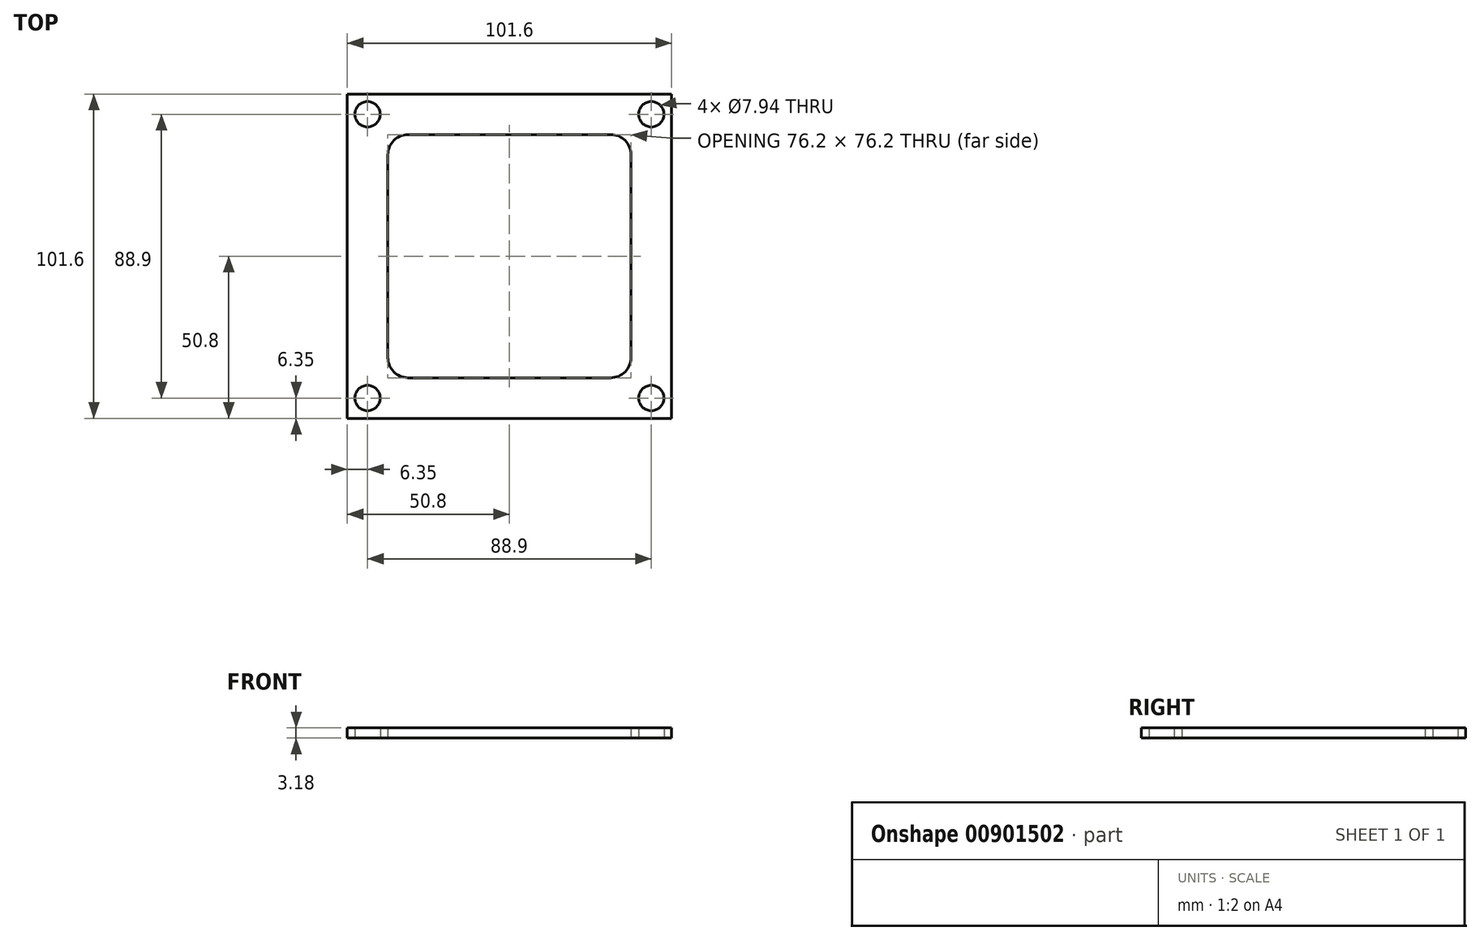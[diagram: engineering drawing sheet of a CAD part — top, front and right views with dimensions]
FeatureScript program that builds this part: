
annotation { "Feature Type Name" : "Feature", "Feature Type Description" : "" }
export const myFeature = defineFeature(function(context is Context, id is Id, definition is map)
    precondition{}
    {
        {
            var Q0;
            Q0=qCreatedBy(makeId("Top.planeOp"),FACE);
            var sketch = newSketch(context, id + "F0", { "sketchPlane" : qUnion([Q0])});
            skLineSegment(sketch, "E0.bottom", {"start": v(0, 0) * mm, "end": v(101.6, 0) * mm});
            skLineSegment(sketch, "E0.top", {"start": v(0, 101.6) * mm, "end": v(101.6, 101.6) * mm});
            skLineSegment(sketch, "E0.left", {"start": v(0, 0) * mm, "end": v(0, 101.6) * mm});
            skLineSegment(sketch, "E0.right", {"start": v(101.6, 0) * mm, "end": v(101.6, 101.6) * mm});
            skLineSegment(sketch, "E1.bottom", {"start": v(19.05, 12.7) * mm, "end": v(82.55, 12.7) * mm});
            skLineSegment(sketch, "E1.top", {"start": v(19.05, 88.9) * mm, "end": v(82.55, 88.9) * mm});
            skLineSegment(sketch, "E1.left", {"start": v(12.7, 19.05) * mm, "end": v(12.7, 82.55) * mm});
            skLineSegment(sketch, "E1.right", {"start": v(88.9, 19.05) * mm, "end": v(88.9, 82.55) * mm});
            skPoint(sketch, "E2.visualSharp", {"position": v(12.7, 12.7) * mm});
            skArc(sketch, "E2.filletArc", {"start": v(12.7, 19.05) * mm, "mid": v(14.56, 14.56) * mm, "end": v(19.05, 12.7) * mm});
            skPoint(sketch, "E3.visualSharp", {"position": v(88.9, 12.7) * mm});
            skArc(sketch, "E3.filletArc", {"start": v(82.55, 12.7) * mm, "mid": v(87.04, 14.56) * mm, "end": v(88.9, 19.05) * mm});
            skPoint(sketch, "E4.visualSharp", {"position": v(88.9, 88.9) * mm});
            skArc(sketch, "E4.filletArc", {"start": v(88.9, 82.55) * mm, "mid": v(87.04, 87.04) * mm, "end": v(82.55, 88.9) * mm});
            skPoint(sketch, "E5.visualSharp", {"position": v(12.7, 88.9) * mm});
            skArc(sketch, "E5.filletArc", {"start": v(19.05, 88.9) * mm, "mid": v(14.56, 87.04) * mm, "end": v(12.7, 82.55) * mm});
            skLineSegment(sketch, "E6", {"start": v(88.9, 12.7) * mm, "end": v(101.6, 0) * mm, "construction": true});
            skLineSegment(sketch, "E7", {"start": v(12.7, 12.7) * mm, "end": v(0, 0) * mm, "construction": true});
            skLineSegment(sketch, "E8", {"start": v(6.35, 6.35) * mm, "end": v(95.25, 6.35) * mm, "construction": true});
            skLineSegment(sketch, "E9", {"start": v(0, 101.6) * mm, "end": v(12.7, 88.9) * mm, "construction": true});
            skLineSegment(sketch, "E10", {"start": v(88.9, 88.9) * mm, "end": v(101.6, 101.6) * mm, "construction": true});
            skLineSegment(sketch, "E11", {"start": v(95.25, 95.25) * mm, "end": v(6.35, 95.25) * mm, "construction": true});
            skLineSegment(sketch, "E12", {"start": v(6.35, 95.25) * mm, "end": v(6.35, 6.35) * mm, "construction": true});
            skLineSegment(sketch, "E13", {"start": v(95.25, 6.35) * mm, "end": v(95.25, 95.25) * mm, "construction": true});
            skCircle(sketch, "E14", {"center": v(6.35, 95.25) * mm, "radius": 3.97 * mm});
            skCircle(sketch, "E15.0.1.0", {"center": v(6.35, 6.35) * mm, "radius": 3.97 * mm});
            skCircle(sketch, "E15.1.0.0", {"center": v(95.25, 95.25) * mm, "radius": 3.97 * mm});
            skCircle(sketch, "E15.1.1.0", {"center": v(95.25, 6.35) * mm, "radius": 3.97 * mm});
            skLineSegment(sketch, "E15.direction1", {"start": v(6.35, 95.25) * mm, "end": v(95.25, 95.25) * mm, "construction": true});
            skLineSegment(sketch, "E16.bottom", {"start": v(2.38, 2.38) * mm, "end": v(10.32, 2.38) * mm, "construction": true});
            skLineSegment(sketch, "E16.top", {"start": v(2.38, 10.32) * mm, "end": v(10.32, 10.32) * mm, "construction": true});
            skLineSegment(sketch, "E16.left", {"start": v(2.38, 2.38) * mm, "end": v(2.38, 10.32) * mm, "construction": true});
            skLineSegment(sketch, "E16.right", {"start": v(10.32, 2.38) * mm, "end": v(10.32, 10.32) * mm, "construction": true});
            skLineSegment(sketch, "E17.0.1.0", {"start": v(10.32, 91.28) * mm, "end": v(10.32, 99.22) * mm, "construction": true});
            skLineSegment(sketch, "E17.0.1.1", {"start": v(2.38, 99.22) * mm, "end": v(10.32, 99.22) * mm, "construction": true});
            skLineSegment(sketch, "E17.0.1.2", {"start": v(2.38, 91.28) * mm, "end": v(2.38, 99.22) * mm, "construction": true});
            skLineSegment(sketch, "E17.0.1.3", {"start": v(2.38, 91.28) * mm, "end": v(10.32, 91.28) * mm, "construction": true});
            skLineSegment(sketch, "E17.1.0.0", {"start": v(99.22, 2.38) * mm, "end": v(99.22, 10.32) * mm, "construction": true});
            skLineSegment(sketch, "E17.1.0.1", {"start": v(91.28, 10.32) * mm, "end": v(99.22, 10.32) * mm, "construction": true});
            skLineSegment(sketch, "E17.1.0.2", {"start": v(91.28, 2.38) * mm, "end": v(91.28, 10.32) * mm, "construction": true});
            skLineSegment(sketch, "E17.1.0.3", {"start": v(91.28, 2.38) * mm, "end": v(99.22, 2.38) * mm, "construction": true});
            skLineSegment(sketch, "E17.1.1.0", {"start": v(99.22, 91.28) * mm, "end": v(99.22, 99.22) * mm, "construction": true});
            skLineSegment(sketch, "E17.1.1.1", {"start": v(91.28, 99.22) * mm, "end": v(99.22, 99.22) * mm, "construction": true});
            skLineSegment(sketch, "E17.1.1.2", {"start": v(91.28, 91.28) * mm, "end": v(91.28, 99.22) * mm, "construction": true});
            skLineSegment(sketch, "E17.1.1.3", {"start": v(91.28, 91.28) * mm, "end": v(99.22, 91.28) * mm, "construction": true});
            skSolve(sketch);
        }
        {
            var Q0;
            Q0=makeQuery(id+"F0.imprint","IMPRINT",FACE,{"disambiguationData":[TD([[makeQuery(id+"F0.imprint","IMPRINT",EDGE,{"derivedFrom":sQuery(id+"F0.wireOp",EDGE,"E0.bottom")}),1.0]])]});
            extrude(context, id + "F1", {"entities" : qUnion([Q0]), "depth" : 3.17 * mm, "offsetDistance" : 25.4 * mm});
        }
    });
